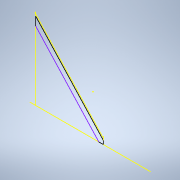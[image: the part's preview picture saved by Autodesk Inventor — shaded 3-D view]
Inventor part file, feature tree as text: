
AUTODESK INVENTOR PART (.ipt)
format: ipt  version: 2021 (Build 250183000, 183)  size: 88,576 bytes
history: native  units: in
note: dims shown in document units (in); Inventor stores cm internally (conversion verified against a paired STEP export)
features: other x6, reference x4, sketch x1
ambient origin geometry x8: Origin, YZ Plane, XZ Plane, XY Plane, X Axis, Y Axis, Z Axis, Center Point
feature tree (11):
  sketch  "Sketch1"
  reference  "Reference1"
  reference  "Reference2"
  reference  "Reference3"
  reference  "Reference4"
  other  "<userpath>\Documents\Inventor CAD\Kerbal Kontroller v.1.iam"
  other  "Kerbal Kontroller v.1.iam"
  other  "Part2:1"
  other  "Part1:1"
  other  "Part4:2"
  other  "Plexi:1"
